# Revit family: Shower-Handshower-KOHLER-PURIST-K-22166BR_1
name_source: partatom
category: Plumbing Fixtures
revit_build: Autodesk Revit 2017 (Build: 20160225_1515(x64)
units: mm (PartAtom-declared; Revit-internal decimal feet)

## family parameters
Cut with Voids When Loaded = No
Host = Face
OmniClass Number = 23.31.17.00
OmniClass Title = Showers
Part Type = Normal
Room Calculation Point = No
Round Connector Dimension = Use Diameter
Shared = No

## types (4) — shared parameters
ADA Compliant = No
Assembly Code = D2010700
CW Connection = No
Cold Water Inlet = Cold Water Inlet
Date Modified = 09/13/2021
Default Elevation = 0"
Description = 284mm multifunctional hand shower
Drain Included = No
Flow Rate = 2 GPM
HW Connection = Yes
Height = 11 3/8"
Hot Water Inlet = Tempered Water Inlet
Length = 3 9/16"
Manufacturer = KOHLER Co.
Master Format 2014 = 22 42 23
Master Format 2014 Name = Residential Showers
Material = Plastic
Pressure = 45.00 psi
Product Name = PURIST
Product Page URL = https://br.kohler.com
URL = https://br.kohler.com
Vent Connection = No
Waste Connection = No
Waste Water Outlet = Waste Water Outlet
WaterSense Certified = No
Width = 5"

## per-type parameters (varying)
| type | Finish | Model | Type |
| CP-Polished Chrome | Kohler-Plastic-CP-Polished_Chrome | K-22166BR-G-CP | 1 |
| BL-Matte Black | Kohler-Plastic-BL-Matte_Black | K-22166BR-G-BL | 2 |
| BN-Vibrant Brushed Nickel | KOHLER-Plastic-BN-Vibrant_Brushed_Nickel | K-22166BR-G-BN | 3 |
| RGD-Polished Rose Gold | Kohler-Plastic-RGD-Polished_Rose_Gold | K-22166BR-G-RGD | 4 |

## geometry (parser evidence)
native form markers: Sweep x6
no freeform markers — native parametric forms only
